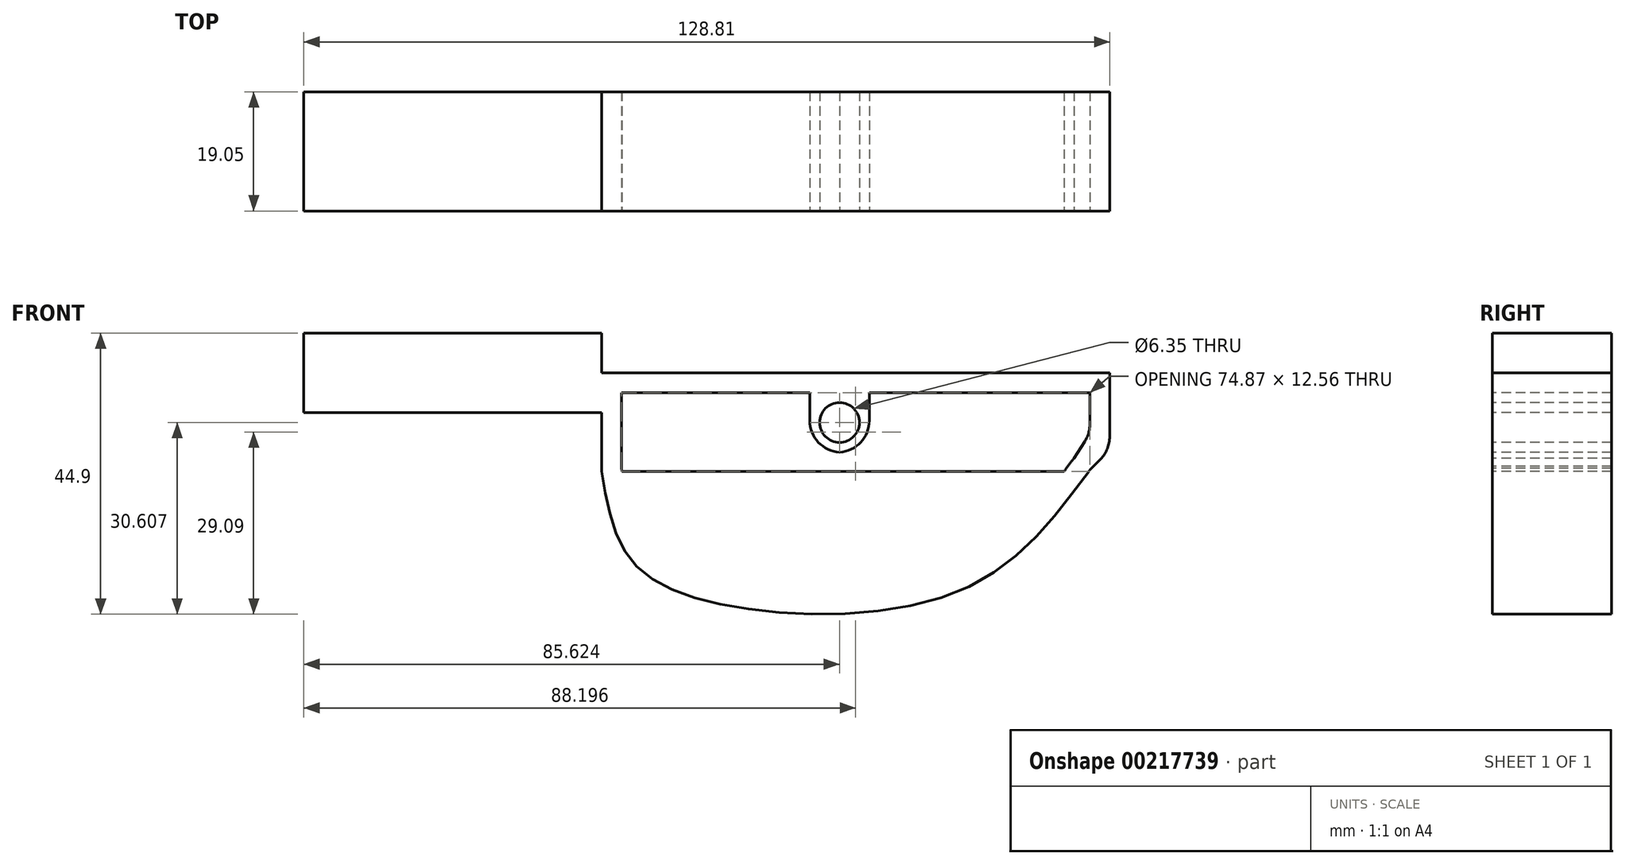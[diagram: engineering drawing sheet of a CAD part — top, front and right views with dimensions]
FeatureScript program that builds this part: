
annotation { "Feature Type Name" : "Feature", "Feature Type Description" : "" }
export const myFeature = defineFeature(function(context is Context, id is Id, definition is map)
    precondition{}
    {
        {
            var Q0;
            Q0=qCreatedBy(makeId("Front.planeOp"),FACE);
            var sketch = newSketch(context, id + "F0", { "sketchPlane" : qUnion([Q0])});
            skLineSegment(sketch, "E0.bottom", {"start": v(25.4, 3.17) * mm, "end": v(-25.4, 3.17) * mm});
            skLineSegment(sketch, "E0.top", {"start": v(25.4, -3.18) * mm, "end": v(-25.4, -3.18) * mm});
            skLineSegment(sketch, "E0.left", {"start": v(25.4, 3.17) * mm, "end": v(25.4, -3.18) * mm});
            skLineSegment(sketch, "E0.right", {"start": v(-25.4, 3.17) * mm, "end": v(-25.4, -3.18) * mm});
            skPoint(sketch, "E0.middle", {"position": v(0, 0) * mm});
            skSolve(sketch);
        }
        {
            var Q0;
            Q0 = qSketchRegion(id + "F0", true);
            extrude(context, id + "F1", {"entities" : qUnion([Q0]), "depth" : 19.05 * mm});
        }
        {
            var Q0;
            Q0=makeQuery(id+"F1.opExtrude","CAP_FACE",FACE,{"disambiguationData":[OSD([sQuery(id+"F0.wireOp",EDGE,"E0.bottom"),sQuery(id+"F0.wireOp",EDGE,"E0.top"),sQuery(id+"F0.wireOp",EDGE,"E0.left"),sQuery(id+"F0.wireOp",EDGE,"E0.right")])],"isStart":false});
            var sketch = newSketch(context, id + "F2", { "sketchPlane" : qUnion([Q0])});
            skLineSegment(sketch, "E1", {"start": v(25.4, -3.18) * mm, "end": v(25.4, -11.77) * mm});
            skLineSegment(sketch, "E2", {"start": v(100.23, -6.54) * mm, "end": v(100.23, 0) * mm});
            skLineSegment(sketch, "E3.0", {"start": v(103.4, -9.1) * mm, "end": v(103.4, 3.17) * mm});
            skLineSegment(sketch, "E4.0", {"start": v(22.23, -3.18) * mm, "end": v(22.23, -12.56) * mm});
            skLineSegment(sketch, "E5", {"start": v(100.23, -12.34) * mm, "end": v(103.4, -9.1) * mm});
            skFitSpline(sketch, "E6", {"points": [v(22.23, -12.56) * mm, v(26.93, -26.78) * mm, v(44.7, -34.44) * mm, v(80.43, -31.22) * mm, v(100.23, -12.34) * mm], "startDerivative": vector(12.8, -79.36) * mm, "endDerivative": vector(61.23, 82.85) * mm});
            skFitSpline(sketch, "E7.0", {"points": [v(25.36, -12.06) * mm, v(25.63, -13.7) * mm, v(26.02, -16.12) * mm, v(26.7, -19.04) * mm, v(27.32, -21.04) * mm, v(28.08, -22.81) * mm, v(28.85, -24.08) * mm, v(29.55, -24.97) * mm, v(30.33, -25.82) * mm, v(31.5, -26.8) * mm, v(33.23, -27.89) * mm, v(35.97, -29.17) * mm, v(39.36, -30.22) * mm, v(43.3, -31.02) * mm, v(46.52, -31.51) * mm, v(49.94, -31.89) * mm, v(54.7, -32.21) * mm, v(59.65, -32.24) * mm, v(64.55, -31.9) * mm, v(68.16, -31.46) * mm, v(71.64, -30.8) * mm, v(74.93, -29.95) * mm, v(77.99, -28.87) * mm, v(80.74, -27.58) * mm, v(83.27, -26.05) * mm, v(85.63, -24.3) * mm, v(87.84, -22.35) * mm, v(90.62, -19.52) * mm, v(93.89, -15.59) * mm, v(96.4, -12.18) * mm, v(97.68, -10.46) * mm]});
            skLineSegment(sketch, "E8", {"start": v(25.4, -11.77) * mm, "end": v(25.36, -12.06) * mm});
            skLineSegment(sketch, "E9", {"start": v(97.68, -10.46) * mm, "end": v(100.23, -6.54) * mm});
            skLineSegment(sketch, "E10", {"start": v(25.4, 3.17) * mm, "end": v(100.23, 3.17) * mm});
            skLineSegment(sketch, "E11", {"start": v(25.4, 3.17) * mm, "end": v(25.4, 0) * mm});
            skLineSegment(sketch, "E12", {"start": v(25.4, 0) * mm, "end": v(100.23, 0) * mm});
            skLineSegment(sketch, "E13", {"start": v(100.23, 3.17) * mm, "end": v(103.4, 3.17) * mm});
            skLineSegment(sketch, "E14", {"start": v(103.4, 3.17) * mm, "end": v(103.4, 0) * mm});
            skLineSegment(sketch, "E15", {"start": v(22.23, -3.18) * mm, "end": v(25.4, -3.18) * mm});
            skLineSegment(sketch, "E16", {"start": v(22.23, -12.56) * mm, "end": v(100.07, -12.56) * mm});
            skFitSpline(sketch, "E17.trimOffspring", {"points": [v(25.36, -12.06) * mm, v(25.63, -13.7) * mm, v(26.02, -16.12) * mm, v(26.7, -19.04) * mm, v(27.32, -21.04) * mm, v(28.08, -22.81) * mm, v(28.85, -24.08) * mm, v(29.55, -24.97) * mm, v(30.33, -25.82) * mm, v(31.5, -26.8) * mm, v(33.23, -27.89) * mm, v(35.97, -29.17) * mm, v(39.36, -30.22) * mm, v(43.3, -31.02) * mm, v(46.52, -31.51) * mm, v(49.94, -31.89) * mm, v(54.7, -32.21) * mm, v(59.65, -32.24) * mm, v(64.55, -31.9) * mm, v(68.16, -31.46) * mm, v(71.64, -30.8) * mm, v(74.93, -29.95) * mm, v(77.99, -28.87) * mm, v(80.74, -27.58) * mm, v(83.27, -26.05) * mm, v(85.63, -24.3) * mm, v(87.84, -22.35) * mm, v(90.62, -19.52) * mm, v(93.89, -15.59) * mm, v(96.4, -12.18) * mm, v(97.68, -10.46) * mm]});
            skSolve(sketch);
        }
        {
            var Q0;
            Q0 = qSketchRegion(id + "F2", true);
            extrude(context, id + "F3", {"entities" : qUnion([Q0]), "operationType" : NewBodyOperationType.ADD, "oppositeDirection" : true, "depth" : 19.05 * mm});
        }
        {
            var Q0;
            Q0 = qSketchRegion(id + "F2", true);
            extrude(context, id + "F4", {"entities" : qUnion([Q0]), "operationType" : NewBodyOperationType.ADD, "oppositeDirection" : true, "depth" : 19.05 * mm});
        }
        {
            var Q0;
            Q0=makeQuery(id+"F3.opExtrude","SWEPT_EDGE",EDGE,{"disambiguationData":[OSD([sQuery(id+"F2.wireOp",EDGE,"E3.0"),sQuery(id+"F2.wireOp",EDGE,"E5")])]});
            var Q1;
            Q1=makeQuery(id+"F3.opExtrude","SWEPT_EDGE",EDGE,{"disambiguationData":[OSD([sQuery(id+"F2.wireOp",EDGE,"E5"),sQuery(id+"F2.wireOp",EDGE,"E6")])]});
            var Q2;
            Q2=makeQuery(id+"F3.opExtrude","SWEPT_EDGE",EDGE,{"disambiguationData":[OSD([sQuery(id+"F2.wireOp",EDGE,"E2"),sQuery(id+"F2.wireOp",EDGE,"E9")])]});
            fillet(context, id + "F5", {"entities" : qUnion([Q0, Q1, Q2]), "radius" : 5.08 * mm, "tangentPropagation" : true, "allowEdgeOverflow" : false});
        }
        {
            var Q0;
            Q0=makeQuery(id+"F3.boolean.opBoolean","MERGE",FACE,{"derivedFrom":[makeQuery(id+"F1.opExtrude","CAP_FACE",FACE,{"disambiguationData":[OSD([sQuery(id+"F0.wireOp",EDGE,"E0.bottom"),sQuery(id+"F0.wireOp",EDGE,"E0.top"),sQuery(id+"F0.wireOp",EDGE,"E0.left"),sQuery(id+"F0.wireOp",EDGE,"E0.right")])],"isStart":false}),makeQuery(id+"F3.opExtrude","CAP_FACE",FACE,{"disambiguationData":[OSD([sQuery(id+"F2.wireOp",EDGE,"E1"),sQuery(id+"F2.wireOp",EDGE,"E2"),sQuery(id+"F2.wireOp",EDGE,"E3.0"),sQuery(id+"F2.wireOp",EDGE,"E4.0"),sQuery(id+"F2.wireOp",EDGE,"E5"),sQuery(id+"F2.wireOp",EDGE,"E6"),sQuery(id+"F2.wireOp",EDGE,"E7.0"),sQuery(id+"F2.wireOp",EDGE,"E8"),sQuery(id+"F2.wireOp",EDGE,"E9"),sQuery(id+"F2.wireOp",EDGE,"E10"),sQuery(id+"F2.wireOp",EDGE,"E11"),sQuery(id+"F2.wireOp",EDGE,"E12"),sQuery(id+"F2.wireOp",EDGE,"E13"),sQuery(id+"F2.wireOp",EDGE,"E14"),sQuery(id+"F2.wireOp",EDGE,"E15")])],"isStart":true})]});
            var sketch = newSketch(context, id + "F6", { "sketchPlane" : qUnion([Q0])});
            skLineSegment(sketch, "E18", {"start": v(-25.4, 3.17) * mm, "end": v(-25.4, 9.52) * mm});
            skLineSegment(sketch, "E19", {"start": v(-25.4, 9.52) * mm, "end": v(22.23, 9.52) * mm});
            skLineSegment(sketch, "E20", {"start": v(22.23, 9.52) * mm, "end": v(22.23, 3.17) * mm});
            skLineSegment(sketch, "E21", {"start": v(22.23, 3.17) * mm, "end": v(-25.4, 3.17) * mm});
            skSolve(sketch);
        }
        {
            var Q0;
            Q0 = qSketchRegion(id + "F6", true);
            extrude(context, id + "F7", {"entities" : qUnion([Q0]), "operationType" : NewBodyOperationType.ADD, "oppositeDirection" : true, "depth" : 19.05 * mm});
        }
        {
            var Q0;
            Q0=makeQuery(id+"F7.boolean.opBoolean","MERGE",FACE,{"derivedFrom":[makeQuery(id+"F3.boolean.opBoolean","MERGE",FACE,{"derivedFrom":[makeQuery(id+"F1.opExtrude","CAP_FACE",FACE,{"disambiguationData":[OSD([sQuery(id+"F0.wireOp",EDGE,"E0.bottom"),sQuery(id+"F0.wireOp",EDGE,"E0.top"),sQuery(id+"F0.wireOp",EDGE,"E0.left"),sQuery(id+"F0.wireOp",EDGE,"E0.right")])],"isStart":false}),makeQuery(id+"F3.opExtrude","CAP_FACE",FACE,{"disambiguationData":[OSD([sQuery(id+"F2.wireOp",EDGE,"E1"),sQuery(id+"F2.wireOp",EDGE,"E2"),sQuery(id+"F2.wireOp",EDGE,"E3.0"),sQuery(id+"F2.wireOp",EDGE,"E4.0"),sQuery(id+"F2.wireOp",EDGE,"E5"),sQuery(id+"F2.wireOp",EDGE,"E6"),sQuery(id+"F2.wireOp",EDGE,"E7.0"),sQuery(id+"F2.wireOp",EDGE,"E8"),sQuery(id+"F2.wireOp",EDGE,"E9"),sQuery(id+"F2.wireOp",EDGE,"E10"),sQuery(id+"F2.wireOp",EDGE,"E11"),sQuery(id+"F2.wireOp",EDGE,"E12"),sQuery(id+"F2.wireOp",EDGE,"E13"),sQuery(id+"F2.wireOp",EDGE,"E14"),sQuery(id+"F2.wireOp",EDGE,"E15")])],"isStart":true})]}),makeQuery(id+"F7.opExtrude","CAP_FACE",FACE,{"disambiguationData":[OSD([sQuery(id+"F6.wireOp",EDGE,"E18"),sQuery(id+"F6.wireOp",EDGE,"E19"),sQuery(id+"F6.wireOp",EDGE,"E20"),sQuery(id+"F6.wireOp",EDGE,"E21")])],"isStart":true})]});
            var sketch = newSketch(context, id + "F8", { "sketchPlane" : qUnion([Q0])});
            skLineSegment(sketch, "E22.bottom", {"start": v(55.46, 0) * mm, "end": v(64.99, 0) * mm});
            skLineSegment(sketch, "E22.top", {"start": v(55.46, -9.53) * mm, "end": v(64.99, -9.53) * mm});
            skLineSegment(sketch, "E22.left", {"start": v(55.46, 0) * mm, "end": v(55.46, -9.53) * mm});
            skLineSegment(sketch, "E22.right", {"start": v(64.99, 0) * mm, "end": v(64.99, -9.53) * mm});
            skCircle(sketch, "E23", {"center": v(60.22, -4.76) * mm, "radius": 3.18 * mm});
            skSolve(sketch);
        }
        {
            var Q0;
            Q0 = qSketchRegion(id + "F8", true);
            extrude(context, id + "F9", {"entities" : qUnion([Q0]), "operationType" : NewBodyOperationType.ADD, "oppositeDirection" : true, "depth" : 19.05 * mm});
        }
        {
            var Q0;
            Q0=makeQuery(id+"F9.opExtrude","SWEPT_EDGE",EDGE,{"disambiguationData":[OSD([sQuery(id+"F8.wireOp",EDGE,"E22.top"),sQuery(id+"F8.wireOp",EDGE,"E22.left")])]});
            var Q1;
            Q1=makeQuery(id+"F9.opExtrude","SWEPT_EDGE",EDGE,{"disambiguationData":[OSD([sQuery(id+"F8.wireOp",EDGE,"E22.top"),sQuery(id+"F8.wireOp",EDGE,"E22.right")])]});
            fillet(context, id + "F10", {"entities" : qUnion([Q0, Q1]), "radius" : 5.08 * mm, "tangentPropagation" : true, "allowEdgeOverflow" : false});
        }
    });
